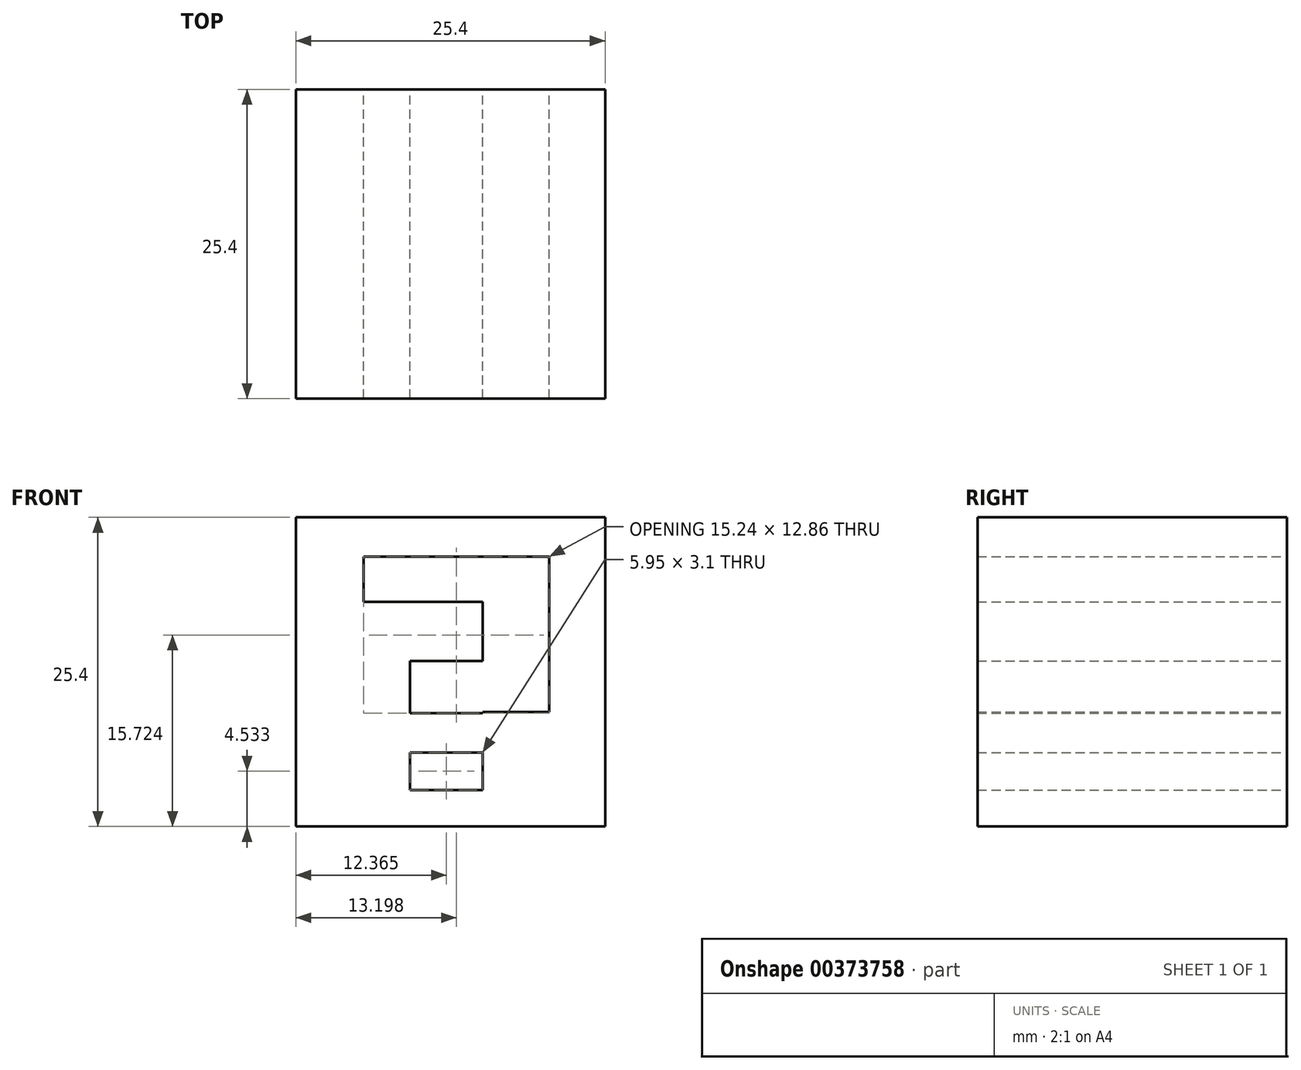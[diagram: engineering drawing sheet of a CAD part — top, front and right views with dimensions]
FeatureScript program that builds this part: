
annotation { "Feature Type Name" : "Feature", "Feature Type Description" : "" }
export const myFeature = defineFeature(function(context is Context, id is Id, definition is map)
    precondition{}
    {
        {
            var Q0;
            Q0=qCreatedBy(makeId("Front.planeOp"),FACE);
            var sketch = newSketch(context, id + "F0", { "sketchPlane" : qUnion([Q0])});
            skLineSegment(sketch, "E0.bottom", {"start": v(-27.94, -24.13) * mm, "end": v(-53.34, -24.13) * mm});
            skLineSegment(sketch, "E0.top", {"start": v(-27.94, -49.53) * mm, "end": v(-53.34, -49.53) * mm});
            skLineSegment(sketch, "E0.left", {"start": v(-27.94, -24.13) * mm, "end": v(-27.94, -49.53) * mm});
            skLineSegment(sketch, "E0.right", {"start": v(-53.34, -24.13) * mm, "end": v(-53.34, -49.53) * mm});
            skLineSegment(sketch, "E1.bottom", {"start": v(-43.95, -46.54) * mm, "end": v(-38, -46.54) * mm});
            skLineSegment(sketch, "E1.top", {"start": v(-43.95, -43.45) * mm, "end": v(-38, -43.45) * mm});
            skLineSegment(sketch, "E1.left", {"start": v(-43.95, -46.54) * mm, "end": v(-43.95, -43.45) * mm});
            skLineSegment(sketch, "E1.right", {"start": v(-38, -46.54) * mm, "end": v(-38, -43.45) * mm});
            skLineSegment(sketch, "E2.bottom", {"start": v(-43.95, -40.23) * mm, "end": v(-38, -40.23) * mm});
            skLineSegment(sketch, "E2.top", {"start": v(-43.95, -35.95) * mm, "end": v(-38, -35.95) * mm});
            skLineSegment(sketch, "E2.left", {"start": v(-43.95, -40.23) * mm, "end": v(-43.95, -35.95) * mm});
            skLineSegment(sketch, "E2.right", {"start": v(-38, -40.23) * mm, "end": v(-38, -35.95) * mm});
            skLineSegment(sketch, "E3.bottom", {"start": v(-38, -35.95) * mm, "end": v(-32.52, -35.95) * mm});
            skLineSegment(sketch, "E3.top", {"start": v(-38, -40.12) * mm, "end": v(-32.52, -40.12) * mm});
            skLineSegment(sketch, "E3.left", {"start": v(-38, -35.95) * mm, "end": v(-38, -40.12) * mm});
            skLineSegment(sketch, "E3.right", {"start": v(-32.52, -35.95) * mm, "end": v(-32.52, -40.12) * mm});
            skLineSegment(sketch, "E4.top", {"start": v(-38, -31.07) * mm, "end": v(-32.52, -31.07) * mm});
            skLineSegment(sketch, "E4.left", {"start": v(-38, -35.95) * mm, "end": v(-38, -31.07) * mm});
            skLineSegment(sketch, "E4.right", {"start": v(-32.52, -35.95) * mm, "end": v(-32.52, -31.07) * mm});
            skLineSegment(sketch, "E5.top", {"start": v(-38, -27.38) * mm, "end": v(-32.52, -27.38) * mm});
            skLineSegment(sketch, "E5.left", {"start": v(-38, -31.07) * mm, "end": v(-38, -27.38) * mm});
            skLineSegment(sketch, "E5.right", {"start": v(-32.52, -31.07) * mm, "end": v(-32.52, -27.38) * mm});
            skLineSegment(sketch, "E6.bottom", {"start": v(-38, -27.38) * mm, "end": v(-43.95, -27.38) * mm});
            skLineSegment(sketch, "E6.top", {"start": v(-38, -31.07) * mm, "end": v(-43.95, -31.07) * mm});
            skLineSegment(sketch, "E6.left", {"start": v(-38, -27.38) * mm, "end": v(-38, -31.07) * mm});
            skLineSegment(sketch, "E6.right", {"start": v(-43.95, -27.38) * mm, "end": v(-43.95, -31.07) * mm});
            skLineSegment(sketch, "E7.bottom", {"start": v(-43.95, -27.38) * mm, "end": v(-47.76, -27.38) * mm});
            skLineSegment(sketch, "E7.top", {"start": v(-43.95, -31.07) * mm, "end": v(-47.76, -31.07) * mm});
            skLineSegment(sketch, "E7.right", {"start": v(-47.76, -27.38) * mm, "end": v(-47.76, -31.07) * mm});
            skSolve(sketch);
        }
        {
            var Q0;
            Q0=makeQuery(id+"F0.imprint","IMPRINT",FACE,{"disambiguationData":[TD([[makeQuery(id+"F0.imprint","IMPRINT",EDGE,{"derivedFrom":sQuery(id+"F0.wireOp",EDGE,"E0.bottom")}),1.0]])]});
            extrude(context, id + "F1", {"entities" : qUnion([Q0]), "depth" : 25.4 * mm});
        }
    });
